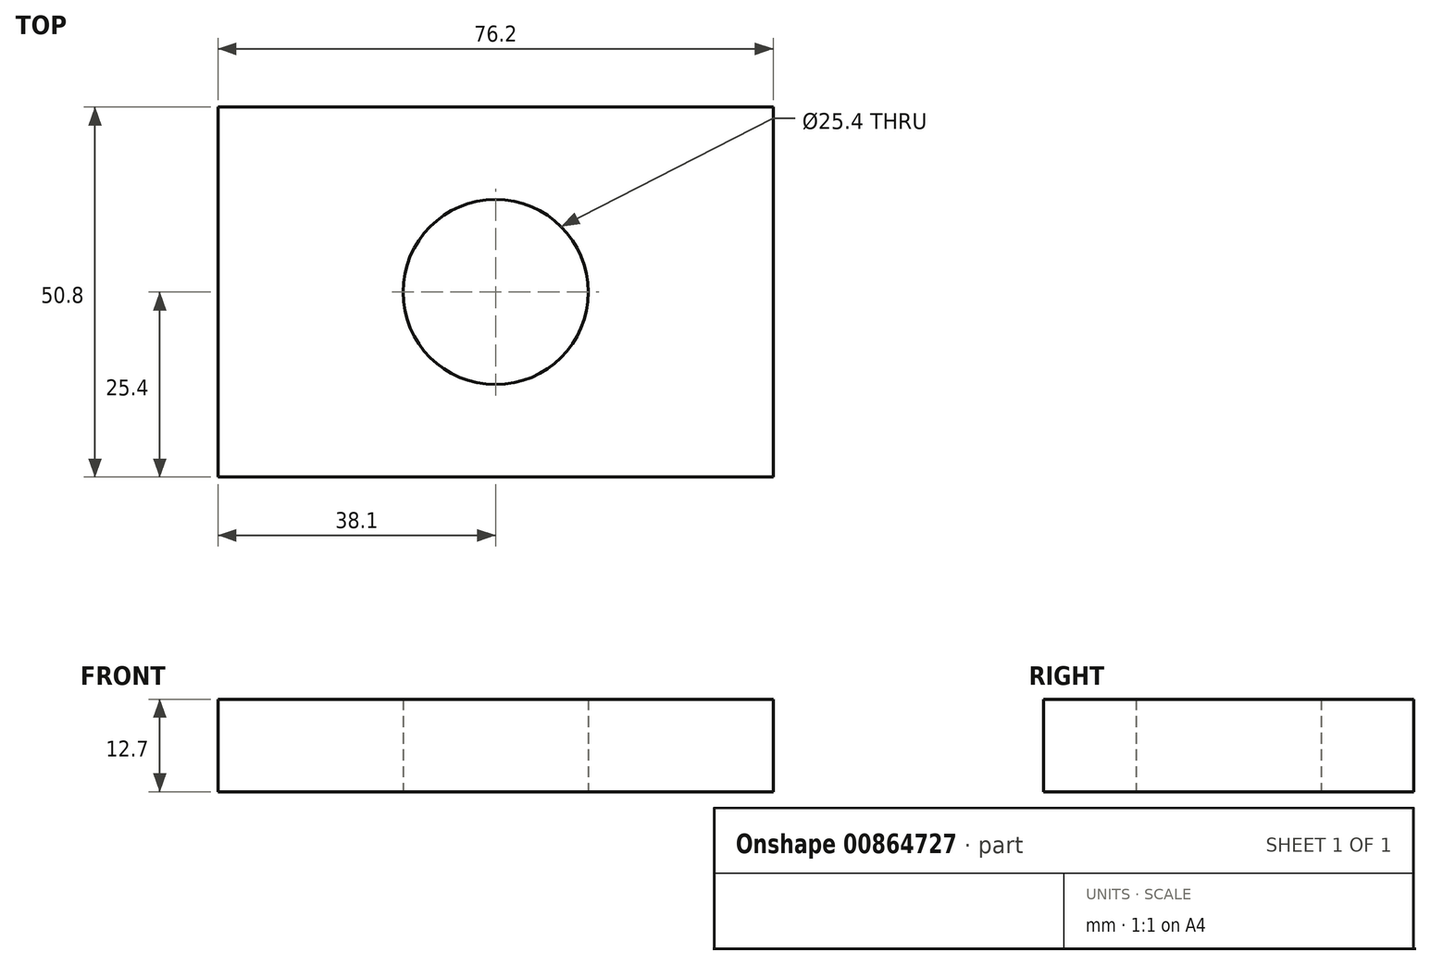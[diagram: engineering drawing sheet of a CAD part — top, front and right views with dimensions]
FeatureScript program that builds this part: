
annotation { "Feature Type Name" : "Feature", "Feature Type Description" : "" }
export const myFeature = defineFeature(function(context is Context, id is Id, definition is map)
    precondition{}
    {
        {
            var Q0;
            Q0=qCreatedBy(makeId("Top.planeOp"),FACE);
            var sketch = newSketch(context, id + "F0", { "sketchPlane" : qUnion([Q0])});
            skLineSegment(sketch, "E0.bottom", {"start": v(38.1, -25.4) * mm, "end": v(-38.1, -25.4) * mm});
            skLineSegment(sketch, "E0.top", {"start": v(38.1, 25.4) * mm, "end": v(-38.1, 25.4) * mm});
            skLineSegment(sketch, "E0.left", {"start": v(38.1, -25.4) * mm, "end": v(38.1, 25.4) * mm});
            skLineSegment(sketch, "E0.right", {"start": v(-38.1, -25.4) * mm, "end": v(-38.1, 25.4) * mm});
            skPoint(sketch, "E0.middle", {"position": v(0, 0) * mm});
            skCircle(sketch, "E1", {"center": v(0, 0) * mm, "radius": 12.7 * mm});
            skSolve(sketch);
        }
        {
            var Q0;
            Q0=makeQuery(id+"F0.imprint","IMPRINT",FACE,{"disambiguationData":[TD([[makeQuery(id+"F0.imprint","IMPRINT",EDGE,{"derivedFrom":sQuery(id+"F0.wireOp",EDGE,"E0.bottom")}),-1.0]])]});
            extrude(context, id + "F1", {"entities" : qUnion([Q0]), "depth" : 12.7 * mm, "offsetDistance" : 25.4 * mm});
        }
    });
